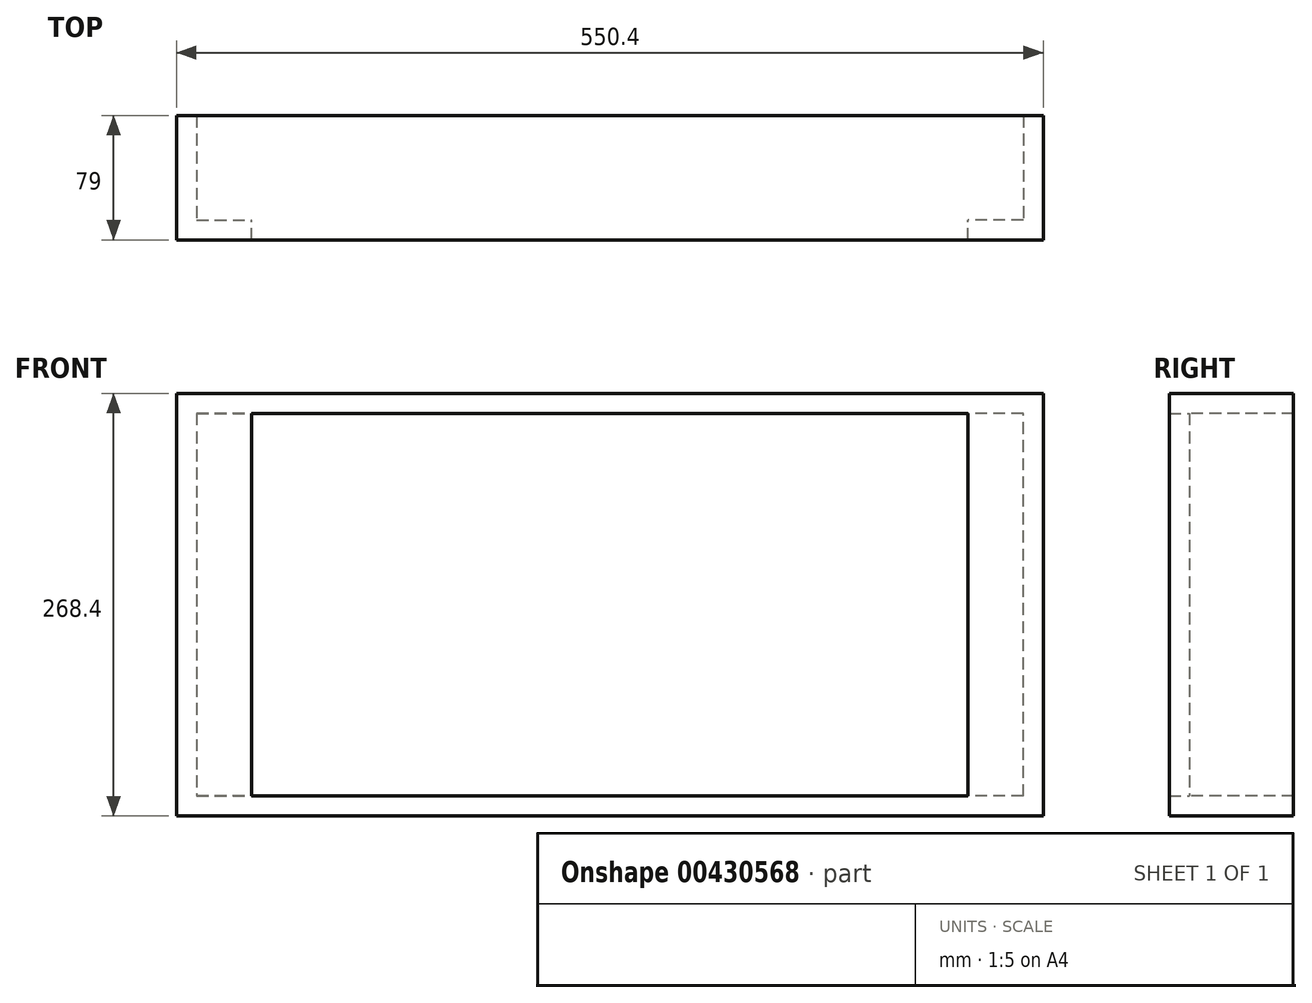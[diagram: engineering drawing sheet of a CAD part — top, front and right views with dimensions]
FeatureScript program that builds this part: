
annotation { "Feature Type Name" : "Feature", "Feature Type Description" : "" }
export const myFeature = defineFeature(function(context is Context, id is Id, definition is map)
    precondition{}
    {
        {
            var Q0;
            Q0=qCreatedBy(makeId("Front.planeOp"),FACE);
            var sketch = newSketch(context, id + "F0", { "sketchPlane" : qUnion([Q0])});
            skLineSegment(sketch, "E0.bottom", {"start": v(262.5, -121.5) * mm, "end": v(-262.5, -121.5) * mm});
            skLineSegment(sketch, "E0.top", {"start": v(262.5, 121.5) * mm, "end": v(-262.5, 121.5) * mm});
            skLineSegment(sketch, "E0.left", {"start": v(262.5, -121.5) * mm, "end": v(262.5, 121.5) * mm});
            skLineSegment(sketch, "E0.right", {"start": v(-262.5, -121.5) * mm, "end": v(-262.5, 121.5) * mm});
            skPoint(sketch, "E0.middle", {"position": v(0, 0) * mm});
            skLineSegment(sketch, "E1.0", {"start": v(275.2, 134.2) * mm, "end": v(-275.2, 134.2) * mm});
            skLineSegment(sketch, "E1.1", {"start": v(275.2, -134.2) * mm, "end": v(275.2, 134.2) * mm});
            skLineSegment(sketch, "E1.2", {"start": v(275.2, -134.2) * mm, "end": v(-275.2, -134.2) * mm});
            skLineSegment(sketch, "E1.3", {"start": v(-275.2, -134.2) * mm, "end": v(-275.2, 134.2) * mm});
            skSolve(sketch);
        }
        {
            var Q0;
            Q0=makeQuery(id+"F0.imprint","IMPRINT",FACE,{"disambiguationData":[TD([[makeQuery(id+"F0.imprint","IMPRINT",EDGE,{"derivedFrom":sQuery(id+"F0.wireOp",EDGE,"E0.bottom")}),1.0]])]});
            extrude(context, id + "F1", {"entities" : qUnion([Q0]), "oppositeDirection" : true, "depth" : 79 * mm});
        }
        {
            var Q0;
            Q0=makeQuery(id+"F1.opExtrude","SWEPT_FACE",FACE,{"disambiguationData":[OSD([sQuery(id+"F0.wireOp",EDGE,"E1.0")])]});
            var sketch = newSketch(context, id + "F2", { "sketchPlane" : qUnion([Q0])});
            skLineSegment(sketch, "E2.bottom", {"start": v(-275.2, 0) * mm, "end": v(-227.5, 0) * mm});
            skLineSegment(sketch, "E2.top", {"start": v(-275.2, 12.7) * mm, "end": v(-227.5, 12.7) * mm});
            skLineSegment(sketch, "E2.left", {"start": v(-275.2, 0) * mm, "end": v(-275.2, 12.7) * mm});
            skLineSegment(sketch, "E2.right", {"start": v(-227.5, 0) * mm, "end": v(-227.5, 12.7) * mm});
            skLineSegment(sketch, "E3.bottom", {"start": v(275.2, 0) * mm, "end": v(227.5, 0) * mm});
            skLineSegment(sketch, "E3.top", {"start": v(275.2, 12.7) * mm, "end": v(227.5, 12.7) * mm});
            skLineSegment(sketch, "E3.left", {"start": v(275.2, 0) * mm, "end": v(275.2, 12.7) * mm});
            skLineSegment(sketch, "E3.right", {"start": v(227.5, 0) * mm, "end": v(227.5, 12.7) * mm});
            skSolve(sketch);
        }
        {
            var Q0;
            Q0=makeQuery(id+"F2.imprint","IMPRINT",FACE,{"disambiguationData":[TD([[makeQuery(id+"F2.imprint","IMPRINT",EDGE,{"derivedFrom":sQuery(id+"F2.wireOp",EDGE,"E2.bottom")}),-1.0]])]});
            var Q1;
            Q1=makeQuery(id+"F2.imprint","IMPRINT",FACE,{"disambiguationData":[TD([[makeQuery(id+"F2.imprint","IMPRINT",EDGE,{"derivedFrom":sQuery(id+"F2.wireOp",EDGE,"E3.bottom")}),-1.0]])]});
            var Q2;
            Q2=makeQuery(id+"F1.opExtrude","SWEPT_FACE",FACE,{"disambiguationData":[OSD([sQuery(id+"F0.wireOp",EDGE,"E1.2")])]});
            extrude(context, id + "F3", {"entities" : qUnion([Q0, Q1]), "operationType" : NewBodyOperationType.ADD, "endBound" : BoundingType.UP_TO_SURFACE, "oppositeDirection" : true, "endBoundEntityFace" : qUnion([Q2]), "depth" : 25 * mm});
        }
    });
